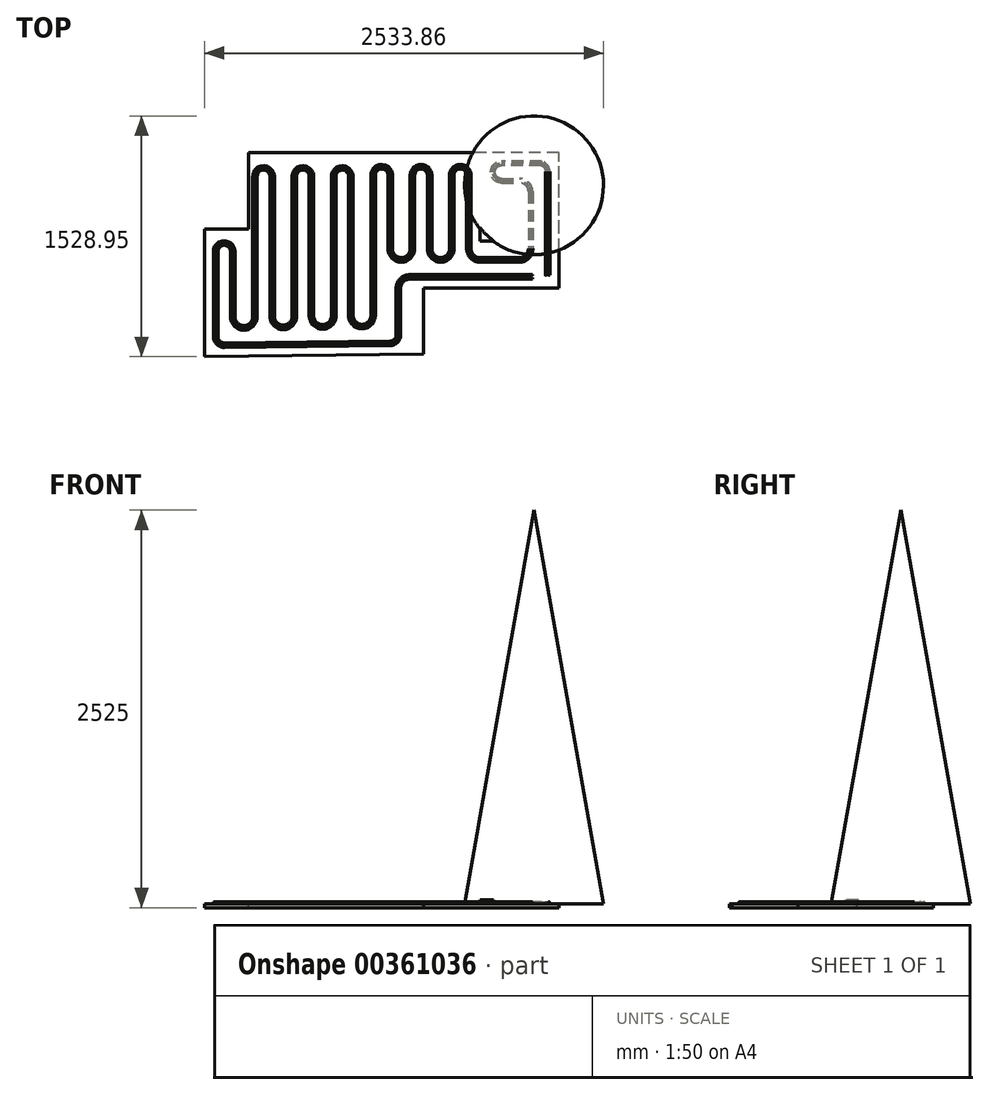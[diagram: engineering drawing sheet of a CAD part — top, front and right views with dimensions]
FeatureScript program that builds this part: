
annotation { "Feature Type Name" : "Feature", "Feature Type Description" : "" }
export const myFeature = defineFeature(function(context is Context, id is Id, definition is map)
    precondition{}
    {
        {
            var Q0;
            Q0=qCreatedBy(makeId("Top.planeOp"),FACE);
            var sketch = newSketch(context, id + "F0", { "sketchPlane" : qUnion([Q0])});
            skLineSegment(sketch, "E0", {"start": v(0, 0) * mm, "end": v(-1970, 0) * mm});
            skLineSegment(sketch, "E1", {"start": v(-1970, 0) * mm, "end": v(-1970, -485) * mm});
            skLineSegment(sketch, "E2", {"start": v(-1970, -485) * mm, "end": v(-2250, -485) * mm});
            skLineSegment(sketch, "E3", {"start": v(-2250, -485) * mm, "end": v(-2250, -1295) * mm});
            skLineSegment(sketch, "E4", {"start": v(-2250, -1295) * mm, "end": v(-860, -1280) * mm});
            skLineSegment(sketch, "E5", {"start": v(-860, -1280) * mm, "end": v(-860, -860) * mm});
            skLineSegment(sketch, "E6", {"start": v(-860, -860) * mm, "end": v(0, -860) * mm});
            skLineSegment(sketch, "E7", {"start": v(0, -860) * mm, "end": v(0, 0) * mm});
            skSolve(sketch);
        }
        {
            var Q0;
            Q0=makeQuery(id+"F0.imprint","IMPRINT",FACE,{"disambiguationData":[TD([[makeQuery(id+"F0.imprint","IMPRINT",EDGE,{"derivedFrom":sQuery(id+"F0.wireOp",EDGE,"E0")}),1.0]])]});
            extrude(context, id + "F1", {"entities" : qUnion([Q0]), "oppositeDirection" : true, "depth" : 25 * mm});
        }
        {
            var Q0;
            Q0=makeQuery(id+"F1.opExtrude","CAP_FACE",FACE,{"disambiguationData":[OSD([sQuery(id+"F0.wireOp",EDGE,"E0"),sQuery(id+"F0.wireOp",EDGE,"E1"),sQuery(id+"F0.wireOp",EDGE,"E2"),sQuery(id+"F0.wireOp",EDGE,"E3"),sQuery(id+"F0.wireOp",EDGE,"E4"),sQuery(id+"F0.wireOp",EDGE,"E5"),sQuery(id+"F0.wireOp",EDGE,"E6"),sQuery(id+"F0.wireOp",EDGE,"E7")])],"isStart":true});
            var sketch = newSketch(context, id + "F2", { "sketchPlane" : qUnion([Q0])});
            skLineSegment(sketch, "E8", {"start": v(-62.5, -1293.51) * mm, "end": v(-62.5, 0) * mm, "construction": true});
            skLineSegment(sketch, "E9.1.0.0", {"start": v(-187.5, -1293.51) * mm, "end": v(-187.5, 0) * mm, "construction": true});
            skLineSegment(sketch, "E9.2.0.0", {"start": v(-312.5, -1293.51) * mm, "end": v(-312.5, 0) * mm, "construction": true});
            skLineSegment(sketch, "E9.3.0.0", {"start": v(-437.5, -1293.51) * mm, "end": v(-437.5, 0) * mm, "construction": true});
            skLineSegment(sketch, "E9.4.0.0", {"start": v(-562.5, -1293.51) * mm, "end": v(-562.5, 0) * mm, "construction": true});
            skLineSegment(sketch, "E9.5.0.0", {"start": v(-687.5, -1293.51) * mm, "end": v(-687.5, 0) * mm, "construction": true});
            skLineSegment(sketch, "E9.6.0.0", {"start": v(-812.5, -1293.51) * mm, "end": v(-812.5, 0) * mm, "construction": true});
            skLineSegment(sketch, "E9.7.0.0", {"start": v(-937.5, -1293.51) * mm, "end": v(-937.5, 0) * mm, "construction": true});
            skLineSegment(sketch, "E9.8.0.0", {"start": v(-1062.5, -1293.51) * mm, "end": v(-1062.5, 0) * mm, "construction": true});
            skLineSegment(sketch, "E9.9.0.0", {"start": v(-1187.5, -1293.51) * mm, "end": v(-1187.5, 0) * mm, "construction": true});
            skLineSegment(sketch, "E9.10.0.0", {"start": v(-1312.5, -1293.51) * mm, "end": v(-1312.5, 0) * mm, "construction": true});
            skLineSegment(sketch, "E9.11.0.0", {"start": v(-1437.5, -1293.51) * mm, "end": v(-1437.5, 0) * mm, "construction": true});
            skLineSegment(sketch, "E9.12.0.0", {"start": v(-1562.5, -1293.51) * mm, "end": v(-1562.5, 0) * mm, "construction": true});
            skLineSegment(sketch, "E9.13.0.0", {"start": v(-1687.5, -1293.51) * mm, "end": v(-1687.5, 0) * mm, "construction": true});
            skLineSegment(sketch, "E9.14.0.0", {"start": v(-1812.5, -1293.51) * mm, "end": v(-1812.5, 0) * mm, "construction": true});
            skLineSegment(sketch, "E9.15.0.0", {"start": v(-1937.5, -1293.51) * mm, "end": v(-1937.5, 0) * mm, "construction": true});
            skLineSegment(sketch, "E9.16.0.0", {"start": v(-2062.5, -1293.51) * mm, "end": v(-2062.5, 0) * mm, "construction": true});
            skLineSegment(sketch, "E9.17.0.0", {"start": v(-2187.5, -1293.51) * mm, "end": v(-2187.5, 0) * mm, "construction": true});
            skLineSegment(sketch, "E9.18.0.0", {"start": v(-2312.5, -1293.51) * mm, "end": v(-2312.5, 0) * mm, "construction": true});
            skLineSegment(sketch, "E9.19.0.0", {"start": v(-2437.5, -1293.51) * mm, "end": v(-2437.5, 0) * mm, "construction": true});
            skLineSegment(sketch, "E9.direction1", {"start": v(-62.5, -1293.51) * mm, "end": v(-187.5, -1293.51) * mm, "construction": true});
            skLineSegment(sketch, "E10", {"start": v(0, -62.5) * mm, "end": v(-2437.5, -62.5) * mm, "construction": true});
            skLineSegment(sketch, "E11.0.1.0", {"start": v(0, -187.5) * mm, "end": v(-2437.5, -187.5) * mm, "construction": true});
            skLineSegment(sketch, "E11.0.2.0", {"start": v(0, -312.5) * mm, "end": v(-2437.5, -312.5) * mm, "construction": true});
            skLineSegment(sketch, "E11.0.3.0", {"start": v(0, -437.5) * mm, "end": v(-2437.5, -437.5) * mm, "construction": true});
            skLineSegment(sketch, "E11.0.4.0", {"start": v(0, -562.5) * mm, "end": v(-2437.5, -562.5) * mm, "construction": true});
            skLineSegment(sketch, "E11.0.5.0", {"start": v(0, -687.5) * mm, "end": v(-2437.5, -687.5) * mm, "construction": true});
            skLineSegment(sketch, "E11.0.6.0", {"start": v(0, -812.5) * mm, "end": v(-2437.5, -812.5) * mm, "construction": true});
            skLineSegment(sketch, "E11.0.7.0", {"start": v(0, -937.5) * mm, "end": v(-2437.5, -937.5) * mm, "construction": true});
            skLineSegment(sketch, "E11.0.8.0", {"start": v(0, -1062.5) * mm, "end": v(-2437.5, -1062.5) * mm, "construction": true});
            skLineSegment(sketch, "E11.0.9.0", {"start": v(0, -1187.5) * mm, "end": v(-2437.5, -1187.5) * mm, "construction": true});
            skLineSegment(sketch, "E11.direction1", {"start": v(-2437.5, -62.5) * mm, "end": v(-2410, -62.5) * mm, "construction": true});
            skLineSegment(sketch, "E11.direction2", {"start": v(-2437.5, -62.5) * mm, "end": v(-2437.5, -187.5) * mm, "construction": true});
            skLineSegment(sketch, "E12", {"start": v(-62.5, -937.5) * mm, "end": v(-62.5, -62.5) * mm});
            skLineSegment(sketch, "E13", {"start": v(-437.5, -672.5) * mm, "end": v(-562.5, -672.5) * mm});
            skLineSegment(sketch, "E14", {"start": v(-562.5, -672.5) * mm, "end": v(-562.5, -62.5) * mm});
            skLineSegment(sketch, "E15", {"start": v(-562.5, -62.5) * mm, "end": v(-687.5, -62.5) * mm});
            skLineSegment(sketch, "E16", {"start": v(-687.5, -62.5) * mm, "end": v(-687.5, -672.5) * mm});
            skLineSegment(sketch, "E17", {"start": v(-687.5, -672.5) * mm, "end": v(-812.5, -672.5) * mm});
            skLineSegment(sketch, "E18", {"start": v(-812.5, -672.5) * mm, "end": v(-812.5, -62.5) * mm});
            skLineSegment(sketch, "E19", {"start": v(-812.5, -62.5) * mm, "end": v(-937.5, -62.5) * mm});
            skLineSegment(sketch, "E20", {"start": v(-937.5, -62.5) * mm, "end": v(-937.5, -672.5) * mm});
            skLineSegment(sketch, "E21", {"start": v(-937.5, -672.5) * mm, "end": v(-1062.5, -672.5) * mm});
            skLineSegment(sketch, "E22", {"start": v(-1062.5, -672.5) * mm, "end": v(-1062.5, -62.5) * mm});
            skLineSegment(sketch, "E23", {"start": v(-1062.5, -62.5) * mm, "end": v(-1187.5, -62.5) * mm});
            skLineSegment(sketch, "E24", {"start": v(-1187.5, -62.5) * mm, "end": v(-1187.5, -1096.02) * mm});
            skLineSegment(sketch, "E25", {"start": v(-1187.5, -1096.02) * mm, "end": v(-1312.5, -1096.02) * mm});
            skLineSegment(sketch, "E26", {"start": v(-1312.5, -1096.02) * mm, "end": v(-1312.5, -62.5) * mm});
            skLineSegment(sketch, "E27", {"start": v(-1312.5, -62.5) * mm, "end": v(-1437.5, -62.5) * mm});
            skLineSegment(sketch, "E28", {"start": v(-1437.5, -62.5) * mm, "end": v(-1437.5, -1098.72) * mm});
            skLineSegment(sketch, "E29", {"start": v(-1437.5, -1098.72) * mm, "end": v(-1562.5, -1098.72) * mm});
            skLineSegment(sketch, "E30", {"start": v(-1562.5, -1098.72) * mm, "end": v(-1562.5, -62.5) * mm});
            skLineSegment(sketch, "E31", {"start": v(-1562.5, -62.5) * mm, "end": v(-1687.5, -62.5) * mm});
            skLineSegment(sketch, "E32", {"start": v(-1687.5, -62.5) * mm, "end": v(-1687.5, -1101.42) * mm});
            skLineSegment(sketch, "E33", {"start": v(-1687.5, -1101.42) * mm, "end": v(-1812.5, -1101.42) * mm});
            skLineSegment(sketch, "E34", {"start": v(-1812.5, -1101.42) * mm, "end": v(-1812.5, -62.5) * mm});
            skLineSegment(sketch, "E35", {"start": v(-1812.5, -62.5) * mm, "end": v(-1937.5, -62.5) * mm});
            skLineSegment(sketch, "E36", {"start": v(-1937.5, -62.5) * mm, "end": v(-1937.5, -1104.12) * mm});
            skLineSegment(sketch, "E37", {"start": v(-1937.5, -1104.12) * mm, "end": v(-2062.5, -1104.12) * mm});
            skLineSegment(sketch, "E38", {"start": v(-2062.5, -547.5) * mm, "end": v(-2187.5, -547.5) * mm});
            skLineSegment(sketch, "E39", {"start": v(-2187.5, -547.5) * mm, "end": v(-2187.5, -1231.82) * mm});
            skLineSegment(sketch, "E40", {"start": v(-2187.5, -1231.82) * mm, "end": v(-1010, -1219.12) * mm});
            skLineSegment(sketch, "E41", {"start": v(-1010, -1219.12) * mm, "end": v(-1010, -797.5) * mm});
            skLineSegment(sketch, "E42", {"start": v(-1010, -797.5) * mm, "end": v(-187.5, -797.5) * mm});
            skLineSegment(sketch, "E43", {"start": v(-187.5, -797.5) * mm, "end": v(-187.5, -937.5) * mm});
            skLineSegment(sketch, "E44", {"start": v(-2062.5, -547.5) * mm, "end": v(-2062.5, -1104.12) * mm});
            skLineSegment(sketch, "E45", {"start": v(-62.5, -62.5) * mm, "end": v(-437.5, -62.5) * mm});
            skLineSegment(sketch, "E46", {"start": v(-437.5, -62.5) * mm, "end": v(-437.5, -187.5) * mm});
            skLineSegment(sketch, "E47", {"start": v(-437.5, -187.5) * mm, "end": v(-187.5, -187.5) * mm});
            skLineSegment(sketch, "E48", {"start": v(-187.5, -187.5) * mm, "end": v(-187.5, -672.5) * mm});
            skLineSegment(sketch, "E49", {"start": v(-187.5, -672.5) * mm, "end": v(-437.5, -672.5) * mm});
            skSolve(sketch);
        }
        {
            var Q0;
            {var subQ0=sQuery(id+"F2.wireOp",EDGE,"o94TWT2M-31Vf-qluU-QspM-yvdoEJApc5KK");Q0=makeQuery(id+"F2.imprint","IMPRINT",FACE,{"disambiguationData":[TD([[makeQuery(id+"F2.imprint","IMPRINT",EDGE,{"derivedFrom":subQ0}),1.0]])]});}
            var Q1;
            Q1 = qConstructionFilter(qBodyType(qCreatedBy(id + "F2" ,EDGE), BodyType.WIRE), ConstructionObject.NO);
            extrude(context, id + "F3", {"entities" : qUnion([Q0]), "bodyType" : ExtendedToolBodyType.SURFACE, "surfaceEntities" : qUnion([Q1]), "depth" : 12 * mm});
        }
        {
            var Q0;
            Q0=makeQuery(id+"F3.opExtrude","SWEPT_EDGE",EDGE,{"disambiguationData":[OSD([sQuery(id+"F2.wireOp",VERTEX,"o94TWT2M-31Vf-qluU-QspM-yvdoEJApc5KK.start")])]});
            var Q1;
            Q1=makeQuery(id+"F3.opExtrude","SWEPT_EDGE",EDGE,{"disambiguationData":[OSD([sQuery(id+"F2.wireOp",VERTEX,"3uiTuNdA-6T9n-bDHV-g5J5-OovVtDSzKxf0.start")])]});
            var Q2;
            Q2=makeQuery(id+"F3.opExtrude","SWEPT_EDGE",EDGE,{"disambiguationData":[OSD([sQuery(id+"F2.wireOp",VERTEX,"RiOLPlBG-YKD5-Dv3i-Ig6h-eSt2upFAfSOZ.start")])]});
            var Q3;
            Q3=makeQuery(id+"F3.opExtrude","SWEPT_EDGE",EDGE,{"disambiguationData":[OSD([sQuery(id+"F2.wireOp",VERTEX,"fgvgJ5WA-tqRb-h4RY-nfcN-i2yzFQp1ZdVO.start")])]});
            var Q4;
            Q4=makeQuery(id+"F3.opExtrude","SWEPT_EDGE",EDGE,{"disambiguationData":[OSD([sQuery(id+"F2.wireOp",VERTEX,"E15.start")])]});
            var Q5;
            Q5=makeQuery(id+"F3.opExtrude","SWEPT_EDGE",EDGE,{"disambiguationData":[OSD([sQuery(id+"F2.wireOp",VERTEX,"E16.start")])]});
            var Q6;
            Q6=makeQuery(id+"F3.opExtrude","SWEPT_EDGE",EDGE,{"disambiguationData":[OSD([sQuery(id+"F2.wireOp",VERTEX,"E19.start")])]});
            var Q7;
            Q7=makeQuery(id+"F3.opExtrude","SWEPT_EDGE",EDGE,{"disambiguationData":[OSD([sQuery(id+"F2.wireOp",VERTEX,"E20.start")])]});
            var Q8;
            Q8=makeQuery(id+"F3.opExtrude","SWEPT_EDGE",EDGE,{"disambiguationData":[OSD([sQuery(id+"F2.wireOp",VERTEX,"E23.start")])]});
            var Q9;
            Q9=makeQuery(id+"F3.opExtrude","SWEPT_EDGE",EDGE,{"disambiguationData":[OSD([sQuery(id+"F2.wireOp",VERTEX,"E24.start")])]});
            var Q10;
            Q10=makeQuery(id+"F3.opExtrude","SWEPT_EDGE",EDGE,{"disambiguationData":[OSD([sQuery(id+"F2.wireOp",VERTEX,"E27.start")])]});
            var Q11;
            Q11=makeQuery(id+"F3.opExtrude","SWEPT_EDGE",EDGE,{"disambiguationData":[OSD([sQuery(id+"F2.wireOp",VERTEX,"E28.start")])]});
            var Q12;
            Q12=makeQuery(id+"F3.opExtrude","SWEPT_EDGE",EDGE,{"disambiguationData":[OSD([sQuery(id+"F2.wireOp",VERTEX,"E31.start")])]});
            var Q13;
            Q13=makeQuery(id+"F3.opExtrude","SWEPT_EDGE",EDGE,{"disambiguationData":[OSD([sQuery(id+"F2.wireOp",VERTEX,"E32.start")])]});
            var Q14;
            Q14=makeQuery(id+"F3.opExtrude","SWEPT_EDGE",EDGE,{"disambiguationData":[OSD([sQuery(id+"F2.wireOp",VERTEX,"E35.start")])]});
            var Q15;
            Q15=makeQuery(id+"F3.opExtrude","SWEPT_EDGE",EDGE,{"disambiguationData":[OSD([sQuery(id+"F2.wireOp",VERTEX,"E36.start")])]});
            var Q16;
            Q16=makeQuery(id+"F3.opExtrude","SWEPT_EDGE",EDGE,{"disambiguationData":[OSD([sQuery(id+"F2.wireOp",VERTEX,"E44.start")])]});
            var Q17;
            Q17=makeQuery(id+"F3.opExtrude","SWEPT_EDGE",EDGE,{"disambiguationData":[OSD([sQuery(id+"F2.wireOp",VERTEX,"E39.start")])]});
            var Q18;
            Q18=makeQuery(id+"F3.opExtrude","SWEPT_EDGE",EDGE,{"disambiguationData":[OSD([sQuery(id+"F2.wireOp",VERTEX,"qBJzUNNh-qAKs-Ri77-QN58-BEaqMge8Y34i.start")])]});
            var Q19;
            Q19=makeQuery(id+"F3.opExtrude","SWEPT_EDGE",EDGE,{"disambiguationData":[OSD([sQuery(id+"F2.wireOp",VERTEX,"nYMLm4uN-mVzM-m0Mm-nZ4a-ShaaZ95DERLO.start")])]});
            var Q20;
            Q20=makeQuery(id+"F3.opExtrude","SWEPT_EDGE",EDGE,{"disambiguationData":[OSD([sQuery(id+"F2.wireOp",VERTEX,"E13.start")])]});
            var Q21;
            Q21=makeQuery(id+"F3.opExtrude","SWEPT_EDGE",EDGE,{"disambiguationData":[OSD([sQuery(id+"F2.wireOp",VERTEX,"E14.start")])]});
            var Q22;
            Q22=makeQuery(id+"F3.opExtrude","SWEPT_EDGE",EDGE,{"disambiguationData":[OSD([sQuery(id+"F2.wireOp",VERTEX,"E17.start")])]});
            var Q23;
            Q23=makeQuery(id+"F3.opExtrude","SWEPT_EDGE",EDGE,{"disambiguationData":[OSD([sQuery(id+"F2.wireOp",VERTEX,"E18.start")])]});
            var Q24;
            Q24=makeQuery(id+"F3.opExtrude","SWEPT_EDGE",EDGE,{"disambiguationData":[OSD([sQuery(id+"F2.wireOp",VERTEX,"E21.start")])]});
            var Q25;
            Q25=makeQuery(id+"F3.opExtrude","SWEPT_EDGE",EDGE,{"disambiguationData":[OSD([sQuery(id+"F2.wireOp",VERTEX,"E22.start")])]});
            var Q26;
            Q26=makeQuery(id+"F3.opExtrude","SWEPT_EDGE",EDGE,{"disambiguationData":[OSD([sQuery(id+"F2.wireOp",VERTEX,"E25.start")])]});
            var Q27;
            Q27=makeQuery(id+"F3.opExtrude","SWEPT_EDGE",EDGE,{"disambiguationData":[OSD([sQuery(id+"F2.wireOp",VERTEX,"E41.start")])]});
            var Q28;
            Q28=makeQuery(id+"F3.opExtrude","SWEPT_EDGE",EDGE,{"disambiguationData":[OSD([sQuery(id+"F2.wireOp",VERTEX,"E42.start")])]});
            var Q29;
            Q29=makeQuery(id+"F3.opExtrude","SWEPT_EDGE",EDGE,{"disambiguationData":[OSD([sQuery(id+"F2.wireOp",VERTEX,"E43.start")])]});
            var Q30;
            Q30=makeQuery(id+"F3.opExtrude","SWEPT_EDGE",EDGE,{"disambiguationData":[OSD([sQuery(id+"F2.wireOp",VERTEX,"E26.start")])]});
            var Q31;
            Q31=makeQuery(id+"F3.opExtrude","SWEPT_EDGE",EDGE,{"disambiguationData":[OSD([sQuery(id+"F2.wireOp",VERTEX,"E29.start")])]});
            var Q32;
            Q32=makeQuery(id+"F3.opExtrude","SWEPT_EDGE",EDGE,{"disambiguationData":[OSD([sQuery(id+"F2.wireOp",VERTEX,"E30.start")])]});
            var Q33;
            Q33=makeQuery(id+"F3.opExtrude","SWEPT_EDGE",EDGE,{"disambiguationData":[OSD([sQuery(id+"F2.wireOp",VERTEX,"E33.start")])]});
            var Q34;
            Q34=makeQuery(id+"F3.opExtrude","SWEPT_EDGE",EDGE,{"disambiguationData":[OSD([sQuery(id+"F2.wireOp",VERTEX,"E34.start")])]});
            var Q35;
            Q35=makeQuery(id+"F3.opExtrude","SWEPT_EDGE",EDGE,{"disambiguationData":[OSD([sQuery(id+"F2.wireOp",VERTEX,"E37.start")])]});
            var Q36;
            Q36=makeQuery(id+"F3.opExtrude","SWEPT_EDGE",EDGE,{"disambiguationData":[OSD([sQuery(id+"F2.wireOp",VERTEX,"E44.end")])]});
            var Q37;
            Q37=makeQuery(id+"F3.opExtrude","SWEPT_EDGE",EDGE,{"disambiguationData":[OSD([sQuery(id+"F2.wireOp",VERTEX,"E40.start")])]});
            var Q38;
            Q38=makeQuery(id+"F3.opExtrude","SWEPT_EDGE",EDGE,{"disambiguationData":[OSD([sQuery(id+"F2.wireOp",VERTEX,"E49.start")])]});
            var Q39;
            Q39=makeQuery(id+"F3.opExtrude","SWEPT_EDGE",EDGE,{"disambiguationData":[OSD([sQuery(id+"F2.wireOp",VERTEX,"E48.start")])]});
            var Q40;
            Q40=makeQuery(id+"F3.opExtrude","SWEPT_EDGE",EDGE,{"disambiguationData":[OSD([sQuery(id+"F2.wireOp",VERTEX,"E47.start")])]});
            var Q41;
            Q41=makeQuery(id+"F3.opExtrude","SWEPT_EDGE",EDGE,{"disambiguationData":[OSD([sQuery(id+"F2.wireOp",VERTEX,"E46.start")])]});
            var Q42;
            Q42=makeQuery(id+"F3.opExtrude","SWEPT_EDGE",EDGE,{"disambiguationData":[OSD([sQuery(id+"F2.wireOp",VERTEX,"E45.start")])]});
            fillet(context, id + "F4", {"entities" : qUnion([Q0, Q1, Q2, Q3, Q4, Q5, Q6, Q7, Q8, Q9, Q10, Q11, Q12, Q13, Q14, Q15, Q16, Q17, Q18, Q19, Q20, Q21, Q22, Q23, Q24, Q25, Q26, Q27, Q28, Q29, Q30, Q31, Q32, Q33, Q34, Q35, Q36, Q37, Q38, Q39, Q40, Q41, Q42]), "radius" : (125 / 2) * mm, "tangentPropagation" : true, "allowEdgeOverflow" : false});
        }
        {
            var Q0;
            Q0=makeQuery(id+"F1.opExtrude","CAP_FACE",FACE,{"disambiguationData":[OSD([sQuery(id+"F0.wireOp",EDGE,"E0"),sQuery(id+"F0.wireOp",EDGE,"E1"),sQuery(id+"F0.wireOp",EDGE,"E2"),sQuery(id+"F0.wireOp",EDGE,"E3"),sQuery(id+"F0.wireOp",EDGE,"E4"),sQuery(id+"F0.wireOp",EDGE,"E5"),sQuery(id+"F0.wireOp",EDGE,"E6"),sQuery(id+"F0.wireOp",EDGE,"E7")])],"isStart":true});
            cPlane(context, id + "F5", {"entities" : qUnion([Q0]), "cplaneType" : CPlaneType.OFFSET, "offset" : 2.5 * mm, "width" : 150 * mm, "height" : 150 * mm});
        }
        {
            var Q0;
            Q0=qCreatedBy(id+"F5.planeOp",FACE);
            var sketch = newSketch(context, id + "F6", { "sketchPlane" : qUnion([Q0])});
            skLineSegment(sketch, "E50.0", {"start": v(-82.5, -119.72) * mm, "end": v(-82.5, -777.5) * mm});
            skArc(sketch, "E50.1", {"start": v(-112.72, -79.03) * mm, "mid": v(-90.88, -94.38) * mm, "end": v(-82.5, -119.72) * mm});
            skLineSegment(sketch, "E50.2", {"start": v(-167.5, -610) * mm, "end": v(-167.5, -248.35) * mm});
            skLineSegment(sketch, "E50.8", {"start": v(-582.5, -142.5) * mm, "end": v(-582.5, -610) * mm});
            skArc(sketch, "E50.9", {"start": v(-667.5, -142.5) * mm, "mid": v(-625, -100) * mm, "end": v(-582.5, -142.5) * mm});
            skLineSegment(sketch, "E50.10", {"start": v(-667.5, -610) * mm, "end": v(-667.5, -142.5) * mm});
            skArc(sketch, "E50.11", {"start": v(-832.5, -610) * mm, "mid": v(-750, -692.5) * mm, "end": v(-667.5, -610) * mm});
            skLineSegment(sketch, "E50.12", {"start": v(-832.5, -142.5) * mm, "end": v(-832.5, -610) * mm});
            skArc(sketch, "E50.13", {"start": v(-917.5, -142.5) * mm, "mid": v(-875, -100) * mm, "end": v(-832.5, -142.5) * mm});
            skLineSegment(sketch, "E50.14", {"start": v(-917.5, -610) * mm, "end": v(-917.5, -142.5) * mm});
            skArc(sketch, "E50.15", {"start": v(-1082.5, -610) * mm, "mid": v(-1000, -692.5) * mm, "end": v(-917.5, -610) * mm});
            skLineSegment(sketch, "E50.16", {"start": v(-1082.5, -142.5) * mm, "end": v(-1082.5, -610) * mm});
            skArc(sketch, "E50.17", {"start": v(-1167.5, -142.5) * mm, "mid": v(-1125, -100) * mm, "end": v(-1082.5, -142.5) * mm});
            skLineSegment(sketch, "E50.18", {"start": v(-1167.5, -1033.52) * mm, "end": v(-1167.5, -142.5) * mm});
            skArc(sketch, "E50.19", {"start": v(-1332.5, -1033.52) * mm, "mid": v(-1250, -1116.02) * mm, "end": v(-1167.5, -1033.52) * mm});
            skLineSegment(sketch, "E50.20", {"start": v(-1332.5, -150) * mm, "end": v(-1332.5, -1033.52) * mm});
            skArc(sketch, "E50.21", {"start": v(-2167.5, -627.5) * mm, "mid": v(-2125, -585) * mm, "end": v(-2082.5, -627.5) * mm});
            skLineSegment(sketch, "E50.22", {"start": v(-2167.5, -1167.97) * mm, "end": v(-2167.5, -627.5) * mm});
            skArc(sketch, "E50.23", {"start": v(-2124.54, -1210.47) * mm, "mid": v(-2154.89, -1198.19) * mm, "end": v(-2167.5, -1167.97) * mm});
            skLineSegment(sketch, "E50.24", {"start": v(-1072.04, -1199.11) * mm, "end": v(-2124.54, -1210.47) * mm});
            skArc(sketch, "E50.25", {"start": v(-1030, -1156.62) * mm, "mid": v(-1042.29, -1186.5) * mm, "end": v(-1072.04, -1199.11) * mm});
            skLineSegment(sketch, "E50.26", {"start": v(-1030, -860) * mm, "end": v(-1030, -1156.62) * mm});
            skLineSegment(sketch, "E50.29", {"start": v(-167.5, -777.5) * mm, "end": v(-947.5, -777.5) * mm});
            skArc(sketch, "E50.30", {"start": v(-947.5, -777.5) * mm, "mid": v(-1005.84, -801.66) * mm, "end": v(-1030, -860) * mm});
            skLineSegment(sketch, "E50.31", {"start": v(-2082.5, -1041.62) * mm, "end": v(-2082.5, -627.5) * mm});
            skArc(sketch, "E50.32", {"start": v(-2082.5, -1041.62) * mm, "mid": v(-2000, -1124.12) * mm, "end": v(-1917.5, -1041.62) * mm});
            skLineSegment(sketch, "E50.33", {"start": v(-1917.5, -1041.62) * mm, "end": v(-1917.5, -150) * mm});
            skArc(sketch, "E50.34", {"start": v(-1917.5, -150) * mm, "mid": v(-1875, -107.5) * mm, "end": v(-1832.5, -150) * mm});
            skLineSegment(sketch, "E50.35", {"start": v(-1832.5, -150) * mm, "end": v(-1832.5, -1038.92) * mm});
            skArc(sketch, "E50.36", {"start": v(-1832.5, -1038.92) * mm, "mid": v(-1750, -1121.42) * mm, "end": v(-1667.5, -1038.92) * mm});
            skLineSegment(sketch, "E50.37", {"start": v(-1667.5, -1038.92) * mm, "end": v(-1667.5, -150) * mm});
            skArc(sketch, "E50.38", {"start": v(-1667.5, -150) * mm, "mid": v(-1625, -107.5) * mm, "end": v(-1582.5, -150) * mm});
            skLineSegment(sketch, "E50.39", {"start": v(-1582.5, -150) * mm, "end": v(-1582.5, -1036.22) * mm});
            skArc(sketch, "E50.40", {"start": v(-1582.5, -1036.22) * mm, "mid": v(-1500, -1118.72) * mm, "end": v(-1417.5, -1036.22) * mm});
            skLineSegment(sketch, "E50.41", {"start": v(-1417.5, -1036.22) * mm, "end": v(-1417.5, -150) * mm});
            skArc(sketch, "E50.42", {"start": v(-1417.5, -150) * mm, "mid": v(-1375, -107.5) * mm, "end": v(-1332.5, -150) * mm});
            skLineSegment(sketch, "E51", {"start": v(-82.5, -777.5) * mm, "end": v(-82.5, -1008.77) * mm, "construction": true});
            skLineSegment(sketch, "E52", {"start": v(-500, -692.5) * mm, "end": v(-250, -692.5) * mm});
            skPoint(sketch, "E52.startSnap0", {"position": v(-750, -692.5) * mm});
            skLineSegment(sketch, "E53", {"start": v(-112.72, -79.03) * mm, "end": v(-363.95, -79.03) * mm});
            skLineSegment(sketch, "E54", {"start": v(-406.45, -121.53) * mm, "end": v(-406.45, -123.35) * mm});
            skLineSegment(sketch, "E55", {"start": v(-363.95, -165.85) * mm, "end": v(-250, -165.85) * mm});
            skPoint(sketch, "E56.visualSharp", {"position": v(-582.5, -692.5) * mm});
            skArc(sketch, "E56.filletArc", {"start": v(-582.5, -610) * mm, "mid": v(-558.34, -668.34) * mm, "end": v(-500, -692.5) * mm});
            skPoint(sketch, "E57.visualSharp", {"position": v(-167.5, -692.5) * mm});
            skArc(sketch, "E57.filletArc", {"start": v(-250, -692.5) * mm, "mid": v(-191.66, -668.34) * mm, "end": v(-167.5, -610) * mm});
            skPoint(sketch, "E58.visualSharp", {"position": v(-167.5, -165.85) * mm});
            skArc(sketch, "E58.filletArc", {"start": v(-167.5, -248.35) * mm, "mid": v(-191.66, -190) * mm, "end": v(-250, -165.85) * mm});
            skPoint(sketch, "E59.visualSharp", {"position": v(-406.45, -165.85) * mm});
            skArc(sketch, "E59.filletArc", {"start": v(-406.45, -123.35) * mm, "mid": v(-394, -153.4) * mm, "end": v(-363.95, -165.85) * mm});
            skPoint(sketch, "E60.visualSharp", {"position": v(-406.45, -79.03) * mm});
            skArc(sketch, "E60.filletArc", {"start": v(-363.95, -79.03) * mm, "mid": v(-394, -91.48) * mm, "end": v(-406.45, -121.53) * mm});
            skSolve(sketch);
        }
        {
            var Q0;
            Q0=makeQuery(id+"F1.opExtrude","CAP_FACE",FACE,{"disambiguationData":[OSD([sQuery(id+"F0.wireOp",EDGE,"E0"),sQuery(id+"F0.wireOp",EDGE,"E1"),sQuery(id+"F0.wireOp",EDGE,"E2"),sQuery(id+"F0.wireOp",EDGE,"E3"),sQuery(id+"F0.wireOp",EDGE,"E4"),sQuery(id+"F0.wireOp",EDGE,"E5"),sQuery(id+"F0.wireOp",EDGE,"E6"),sQuery(id+"F0.wireOp",EDGE,"E7")])],"isStart":true});
            cPlane(context, id + "F7", {"entities" : qUnion([Q0]), "cplaneType" : CPlaneType.OFFSET, "offset" : 6 * mm, "width" : 150 * mm, "height" : 150 * mm});
        }
        {
            var Q0;
            Q0=qCreatedBy(id+"F7.planeOp",FACE);
            var sketch = newSketch(context, id + "F8", { "sketchPlane" : qUnion([Q0])});
            skArc(sketch, "E61.0.1", {"start": v(-62.5, -125) * mm, "mid": v(-125, -62.5) * mm, "end": v(-187.5, -125) * mm});
            skArc(sketch, "E61.0.3", {"start": v(-187.5, -125) * mm, "mid": v(-125, -62.5) * mm, "end": v(-62.5, -125) * mm});
            skArc(sketch, "E61.1.1", {"start": v(-187.5, -550) * mm, "mid": v(-250, -612.5) * mm, "end": v(-312.5, -550) * mm});
            skArc(sketch, "E61.1.3", {"start": v(-312.5, -550) * mm, "mid": v(-250, -612.5) * mm, "end": v(-187.5, -550) * mm});
            skArc(sketch, "E61.2.1", {"start": v(-312.5, -125) * mm, "mid": v(-375, -62.5) * mm, "end": v(-437.5, -125) * mm});
            skArc(sketch, "E61.2.3", {"start": v(-437.5, -125) * mm, "mid": v(-375, -62.5) * mm, "end": v(-312.5, -125) * mm});
            skArc(sketch, "E61.3.1", {"start": v(-437.5, -550) * mm, "mid": v(-500, -612.5) * mm, "end": v(-562.5, -550) * mm});
            skArc(sketch, "E61.3.3", {"start": v(-562.5, -550) * mm, "mid": v(-500, -612.5) * mm, "end": v(-437.5, -550) * mm});
            skArc(sketch, "E61.4.1", {"start": v(-562.5, -125) * mm, "mid": v(-625, -62.5) * mm, "end": v(-687.5, -125) * mm});
            skArc(sketch, "E61.4.3", {"start": v(-687.5, -125) * mm, "mid": v(-625, -62.5) * mm, "end": v(-562.5, -125) * mm});
            skArc(sketch, "E61.5.1", {"start": v(-687.5, -550) * mm, "mid": v(-750, -612.5) * mm, "end": v(-812.5, -550) * mm});
            skArc(sketch, "E61.5.3", {"start": v(-812.5, -550) * mm, "mid": v(-750, -612.5) * mm, "end": v(-687.5, -550) * mm});
            skArc(sketch, "E61.6.1", {"start": v(-812.5, -125) * mm, "mid": v(-875, -62.5) * mm, "end": v(-937.5, -125) * mm});
            skArc(sketch, "E61.6.3", {"start": v(-937.5, -125) * mm, "mid": v(-875, -62.5) * mm, "end": v(-812.5, -125) * mm});
            skArc(sketch, "E61.7.1", {"start": v(-937.5, -954.48) * mm, "mid": v(-1000, -1016.98) * mm, "end": v(-1062.5, -954.48) * mm});
            skArc(sketch, "E61.7.3", {"start": v(-1062.5, -954.48) * mm, "mid": v(-1000, -1016.98) * mm, "end": v(-937.5, -954.48) * mm});
            skArc(sketch, "E61.8.1", {"start": v(-1062.5, -125) * mm, "mid": v(-1125, -62.5) * mm, "end": v(-1187.5, -125) * mm});
            skArc(sketch, "E61.8.3", {"start": v(-1187.5, -125) * mm, "mid": v(-1125, -62.5) * mm, "end": v(-1062.5, -125) * mm});
            skArc(sketch, "E61.9.1", {"start": v(-1187.5, -962.81) * mm, "mid": v(-1250, -1025.31) * mm, "end": v(-1312.5, -962.81) * mm});
            skArc(sketch, "E61.9.3", {"start": v(-1312.5, -962.81) * mm, "mid": v(-1250, -1025.31) * mm, "end": v(-1187.5, -962.81) * mm});
            skArc(sketch, "E61.10.1", {"start": v(-1312.5, -125) * mm, "mid": v(-1375, -62.5) * mm, "end": v(-1437.5, -125) * mm});
            skArc(sketch, "E61.10.3", {"start": v(-1437.5, -125) * mm, "mid": v(-1375, -62.5) * mm, "end": v(-1312.5, -125) * mm});
            skArc(sketch, "E61.11.1", {"start": v(-1437.5, -971.15) * mm, "mid": v(-1500, -1033.65) * mm, "end": v(-1562.5, -971.15) * mm});
            skArc(sketch, "E61.11.3", {"start": v(-1562.5, -971.15) * mm, "mid": v(-1500, -1033.65) * mm, "end": v(-1437.5, -971.15) * mm});
            skArc(sketch, "E61.12.1", {"start": v(-1562.5, -125) * mm, "mid": v(-1625, -62.5) * mm, "end": v(-1687.5, -125) * mm});
            skArc(sketch, "E61.12.3", {"start": v(-1687.5, -125) * mm, "mid": v(-1625, -62.5) * mm, "end": v(-1562.5, -125) * mm});
            skArc(sketch, "E61.13.1", {"start": v(-1687.5, -979.48) * mm, "mid": v(-1750, -1041.98) * mm, "end": v(-1812.5, -979.48) * mm});
            skArc(sketch, "E61.13.3", {"start": v(-1812.5, -979.48) * mm, "mid": v(-1750, -1041.98) * mm, "end": v(-1687.5, -979.48) * mm});
            skArc(sketch, "E61.14.1", {"start": v(-1812.5, -125) * mm, "mid": v(-1875, -62.5) * mm, "end": v(-1937.5, -125) * mm});
            skArc(sketch, "E61.14.3", {"start": v(-1937.5, -125) * mm, "mid": v(-1875, -62.5) * mm, "end": v(-1812.5, -125) * mm});
            skArc(sketch, "E61.15.1", {"start": v(-1937.5, -987.81) * mm, "mid": v(-2000, -1050.31) * mm, "end": v(-2062.5, -987.81) * mm});
            skArc(sketch, "E61.15.3", {"start": v(-2062.5, -987.81) * mm, "mid": v(-2000, -1050.31) * mm, "end": v(-1937.5, -987.81) * mm});
            skArc(sketch, "E61.16.0", {"start": v(-2187.5, -610) * mm, "mid": v(-2125, -547.5) * mm, "end": v(-2062.5, -610) * mm});
            skArc(sketch, "E61.16.2", {"start": v(-2062.5, -610) * mm, "mid": v(-2125, -547.5) * mm, "end": v(-2187.5, -610) * mm});
            skArc(sketch, "E61.17.0", {"start": v(-2187.5, -1168.64) * mm, "mid": v(-2168.96, -1213.08) * mm, "end": v(-2124.33, -1231.14) * mm});
            skArc(sketch, "E61.17.2", {"start": v(-2124.33, -1231.14) * mm, "mid": v(-2168.96, -1213.08) * mm, "end": v(-2187.5, -1168.64) * mm});
            skArc(sketch, "E61.18.0", {"start": v(-1071.83, -1219.78) * mm, "mid": v(-1028.07, -1201.24) * mm, "end": v(-1010, -1157.29) * mm});
            skArc(sketch, "E61.18.2", {"start": v(-1010, -1157.29) * mm, "mid": v(-1028.07, -1201.24) * mm, "end": v(-1071.83, -1219.78) * mm});
            skArc(sketch, "E61.19.0", {"start": v(-1010, -860) * mm, "mid": v(-991.7, -815.8) * mm, "end": v(-947.5, -797.5) * mm});
            skArc(sketch, "E61.19.2", {"start": v(-947.5, -797.5) * mm, "mid": v(-991.7, -815.8) * mm, "end": v(-1010, -860) * mm});
            skArc(sketch, "E61.20.0", {"start": v(-250, -797.5) * mm, "mid": v(-205.8, -815.8) * mm, "end": v(-187.5, -860) * mm});
            skArc(sketch, "E61.20.2", {"start": v(-187.5, -860) * mm, "mid": v(-205.8, -815.8) * mm, "end": v(-250, -797.5) * mm});
            skLineSegment(sketch, "E61.21.0", {"start": v(-62.5, -937.5) * mm, "end": v(-62.5, -125) * mm});
            skLineSegment(sketch, "E61.21.2", {"start": v(-62.5, -125) * mm, "end": v(-62.5, -937.5) * mm});
            skLineSegment(sketch, "E61.22.0", {"start": v(-187.5, -125) * mm, "end": v(-187.5, -550) * mm});
            skLineSegment(sketch, "E61.22.2", {"start": v(-187.5, -550) * mm, "end": v(-187.5, -125) * mm});
            skLineSegment(sketch, "E61.23.0", {"start": v(-312.5, -550) * mm, "end": v(-312.5, -125) * mm});
            skLineSegment(sketch, "E61.23.2", {"start": v(-312.5, -125) * mm, "end": v(-312.5, -550) * mm});
            skLineSegment(sketch, "E61.24.0", {"start": v(-437.5, -125) * mm, "end": v(-437.5, -550) * mm});
            skLineSegment(sketch, "E61.24.2", {"start": v(-437.5, -550) * mm, "end": v(-437.5, -125) * mm});
            skLineSegment(sketch, "E61.25.0", {"start": v(-562.5, -550) * mm, "end": v(-562.5, -125) * mm});
            skLineSegment(sketch, "E61.25.2", {"start": v(-562.5, -125) * mm, "end": v(-562.5, -550) * mm});
            skLineSegment(sketch, "E61.26.0", {"start": v(-687.5, -125) * mm, "end": v(-687.5, -550) * mm});
            skLineSegment(sketch, "E61.26.2", {"start": v(-687.5, -550) * mm, "end": v(-687.5, -125) * mm});
            skLineSegment(sketch, "E61.27.0", {"start": v(-812.5, -550) * mm, "end": v(-812.5, -125) * mm});
            skLineSegment(sketch, "E61.27.2", {"start": v(-812.5, -125) * mm, "end": v(-812.5, -550) * mm});
            skLineSegment(sketch, "E61.28.0", {"start": v(-937.5, -125) * mm, "end": v(-937.5, -954.48) * mm});
            skLineSegment(sketch, "E61.28.2", {"start": v(-937.5, -954.48) * mm, "end": v(-937.5, -125) * mm});
            skLineSegment(sketch, "E61.29.0", {"start": v(-1062.5, -954.48) * mm, "end": v(-1062.5, -125) * mm});
            skLineSegment(sketch, "E61.29.2", {"start": v(-1062.5, -125) * mm, "end": v(-1062.5, -954.48) * mm});
            skLineSegment(sketch, "E61.30.0", {"start": v(-1187.5, -125) * mm, "end": v(-1187.5, -962.81) * mm});
            skLineSegment(sketch, "E61.30.2", {"start": v(-1187.5, -962.81) * mm, "end": v(-1187.5, -125) * mm});
            skLineSegment(sketch, "E61.31.0", {"start": v(-1312.5, -962.81) * mm, "end": v(-1312.5, -125) * mm});
            skLineSegment(sketch, "E61.31.2", {"start": v(-1312.5, -125) * mm, "end": v(-1312.5, -962.81) * mm});
            skLineSegment(sketch, "E61.32.0", {"start": v(-1437.5, -125) * mm, "end": v(-1437.5, -971.15) * mm});
            skLineSegment(sketch, "E61.32.2", {"start": v(-1437.5, -971.15) * mm, "end": v(-1437.5, -125) * mm});
            skLineSegment(sketch, "E61.33.0", {"start": v(-1562.5, -971.15) * mm, "end": v(-1562.5, -125) * mm});
            skLineSegment(sketch, "E61.33.2", {"start": v(-1562.5, -125) * mm, "end": v(-1562.5, -971.15) * mm});
            skLineSegment(sketch, "E61.34.0", {"start": v(-1687.5, -125) * mm, "end": v(-1687.5, -979.48) * mm});
            skLineSegment(sketch, "E61.34.2", {"start": v(-1687.5, -979.48) * mm, "end": v(-1687.5, -125) * mm});
            skLineSegment(sketch, "E61.35.0", {"start": v(-1812.5, -979.48) * mm, "end": v(-1812.5, -125) * mm});
            skLineSegment(sketch, "E61.35.2", {"start": v(-1812.5, -125) * mm, "end": v(-1812.5, -979.48) * mm});
            skLineSegment(sketch, "E61.36.0", {"start": v(-1937.5, -125) * mm, "end": v(-1937.5, -987.81) * mm});
            skLineSegment(sketch, "E61.36.2", {"start": v(-1937.5, -987.81) * mm, "end": v(-1937.5, -125) * mm});
            skLineSegment(sketch, "E61.37.0", {"start": v(-2187.5, -1168.64) * mm, "end": v(-2187.5, -610) * mm});
            skLineSegment(sketch, "E61.37.2", {"start": v(-2187.5, -610) * mm, "end": v(-2187.5, -1168.64) * mm});
            skLineSegment(sketch, "E61.38.0", {"start": v(-1071.83, -1219.78) * mm, "end": v(-2124.33, -1231.14) * mm});
            skLineSegment(sketch, "E61.38.2", {"start": v(-2124.33, -1231.14) * mm, "end": v(-1071.83, -1219.78) * mm});
            skLineSegment(sketch, "E61.39.0", {"start": v(-1010, -860) * mm, "end": v(-1010, -1157.29) * mm});
            skLineSegment(sketch, "E61.39.2", {"start": v(-1010, -1157.29) * mm, "end": v(-1010, -860) * mm});
            skLineSegment(sketch, "E61.40.0", {"start": v(-250, -797.5) * mm, "end": v(-947.5, -797.5) * mm});
            skLineSegment(sketch, "E61.40.2", {"start": v(-947.5, -797.5) * mm, "end": v(-250, -797.5) * mm});
            skLineSegment(sketch, "E61.41.0", {"start": v(-187.5, -937.5) * mm, "end": v(-187.5, -860) * mm});
            skLineSegment(sketch, "E61.41.2", {"start": v(-187.5, -860) * mm, "end": v(-187.5, -937.5) * mm});
            skLineSegment(sketch, "E61.42.0", {"start": v(-2062.5, -987.81) * mm, "end": v(-2062.5, -610) * mm});
            skLineSegment(sketch, "E61.42.2", {"start": v(-2062.5, -987.81) * mm, "end": v(-2062.5, -610) * mm});
            skSolve(sketch);
        }
        {
            var Q0;
            Q0=sQuery(id+"F6.wireOp",VERTEX,"E50.0.end");
            var Q1;
            Q1=sQuery(id+"F6.wireOp",EDGE,"E50.0");
            cPlane(context, id + "F9", {"entities" : qUnion([Q0, Q1]), "cplaneType" : CPlaneType.LINE_POINT, "offset" : 25 * mm, "width" : 150 * mm, "height" : 150 * mm});
        }
        {
            var Q0;
            Q0=qCreatedBy(id+"F9.planeOp",FACE);
            var sketch = newSketch(context, id + "F10", { "sketchPlane" : qUnion([Q0])});
            skCircle(sketch, "E62", {"center": v(-82.5, 2.5) * mm, "radius": 2.5 * mm});
            skSolve(sketch);
        }
        {
            var Q0;
            Q0=makeQuery(id+"F10.imprint","IMPRINT",FACE,{"disambiguationData":[TD([[makeQuery(id+"F10.imprint","IMPRINT",EDGE,{"derivedFrom":sQuery(id+"F10.wireOp",EDGE,"E62")}),1.0]])]});
            var Q1;
            Q1 = qConstructionFilter(qBodyType(qCreatedBy(id + "F6" ,EDGE), BodyType.WIRE), ConstructionObject.NO);
            sweep(context, id + "F11", {"profiles" : qUnion([Q0]), "path" : qUnion([Q1])});
        }
        {
            var Q0;
            Q0=qCreatedBy(makeId("Top.planeOp"),FACE);
            cPlane(context, id + "F12", {"entities" : qUnion([Q0]), "cplaneType" : CPlaneType.OFFSET, "offset" : 2500 * mm, "width" : 150 * mm, "height" : 150 * mm});
        }
        {
            var Q0;
            Q0=qCreatedBy(id+"F12.planeOp",FACE);
            var sketch = newSketch(context, id + "F13", { "sketchPlane" : qUnion([Q0])});
            skPoint(sketch, "E63", {"position": v(-156.96, -206.87) * mm});
            skPoint(sketch, "E64", {"position": v(-1260.18, -206.87) * mm});
            skPoint(sketch, "E65", {"position": v(-1765.1, -877.28) * mm});
            skPoint(sketch, "E66", {"position": v(-1260.18, -877.28) * mm});
            skPoint(sketch, "E67", {"position": v(-776.46, -643.9) * mm});
            skSolve(sketch);
        }
        {
            var Q0;
            Q0=qCreatedBy(makeId("Top.planeOp"),FACE);
            var sketch = newSketch(context, id + "F14", { "sketchPlane" : qUnion([Q0])});
            skLineSegment(sketch, "E68.0", {"start": v(-2250, -485) * mm, "end": v(-2250, -1295) * mm});
            skLineSegment(sketch, "E69.0", {"start": v(-1970, -485) * mm, "end": v(-2250, -485) * mm});
            skLineSegment(sketch, "E70.0", {"start": v(-1970, 0) * mm, "end": v(-1970, -485) * mm});
            skLineSegment(sketch, "E71.0", {"start": v(0, 0) * mm, "end": v(-1970, 0) * mm});
            skLineSegment(sketch, "E72.0", {"start": v(0, -860) * mm, "end": v(0, 0) * mm});
            skLineSegment(sketch, "E73.0", {"start": v(-860, -860) * mm, "end": v(0, -860) * mm});
            skLineSegment(sketch, "E74.0", {"start": v(-860, -1280) * mm, "end": v(-860, -860) * mm});
            skLineSegment(sketch, "E75", {"start": v(-2250, -1295) * mm, "end": v(-1510, -1287.01) * mm});
            skLineSegment(sketch, "E76", {"start": v(-860, -1280) * mm, "end": v(-910, -1280.54) * mm});
            skSolve(sketch);
        }
        {
            var Q0;
            Q0 = qSketchRegion(id + "F14", true);
            var Q1;
            Q1 = qConstructionFilter(qBodyType(qCreatedBy(id + "F14" ,EDGE), BodyType.WIRE), ConstructionObject.NO);
            var Q2;
            Q2=qCreatedBy(id+"F12.planeOp",FACE);
            extrude(context, id + "F15", {"entities" : qUnion([Q0]), "bodyType" : ExtendedToolBodyType.SURFACE, "surfaceEntities" : qUnion([Q1]), "endBound" : BoundingType.UP_TO_SURFACE, "endBoundEntityFace" : qUnion([Q2]), "depth" : 25 * mm});
        }
        {
            var Q0;
            Q0=makeQuery(id+"F15.opExtrude","SWEPT_FACE",FACE,{"disambiguationData":[OSD([sQuery(id+"F14.wireOp",EDGE,"E72.0")])]});
            var Q1;
            Q1=sQuery(id+"F13.wireOp",VERTEX,"E63");
            cPlane(context, id + "F16", {"entities" : qUnion([Q0, Q1]), "cplaneType" : CPlaneType.PLANE_POINT, "offset" : 25 * mm, "width" : 150 * mm, "height" : 150 * mm});
        }
        {
            var Q0;
            Q0=qCreatedBy(id+"F16.planeOp",FACE);
            var sketch = newSketch(context, id + "F17", { "sketchPlane" : qUnion([Q0])});
            skLineSegment(sketch, "E77", {"start": v(-206.87, 2500) * mm, "end": v(-206.87, 0) * mm, "construction": true});
            skLineSegment(sketch, "E78", {"start": v(-206.87, 2500) * mm, "end": v(233.95, 0) * mm});
            skLineSegment(sketch, "E79", {"start": v(233.95, 0) * mm, "end": v(-206.87, 0) * mm});
            skLineSegment(sketch, "E80", {"start": v(-206.87, 2500) * mm, "end": v(-647.68, 0) * mm, "construction": true});
            skLineSegment(sketch, "E81", {"start": v(-647.68, 0) * mm, "end": v(-206.87, 0) * mm, "construction": true});
            skLineSegment(sketch, "E82", {"start": v(-206.87, 0) * mm, "end": v(-206.87, 2500) * mm});
            skSolve(sketch);
        }
        {
            var Q0;
            Q0=makeQuery(id+"F17.imprint","IMPRINT",FACE,{"disambiguationData":[TD([[makeQuery(id+"F17.imprint","IMPRINT",EDGE,{"derivedFrom":sQuery(id+"F17.wireOp",EDGE,"E78")}),-1.0]])]});
            var Q1;
            Q1=sQuery(id+"F17.wireOp",EDGE,"E82");
            revolve(context, id + "F18", {"entities" : qUnion([Q0]), "axis" : qUnion([Q1]), "revolveType" : RevolveType.FULL});
        }
        {
            var Q0;
            Q0=makeQuery(id+"F1.opExtrude","CAP_FACE",FACE,{"disambiguationData":[OSD([sQuery(id+"F0.wireOp",EDGE,"E0"),sQuery(id+"F0.wireOp",EDGE,"E1"),sQuery(id+"F0.wireOp",EDGE,"E2"),sQuery(id+"F0.wireOp",EDGE,"E3"),sQuery(id+"F0.wireOp",EDGE,"E4"),sQuery(id+"F0.wireOp",EDGE,"E5"),sQuery(id+"F0.wireOp",EDGE,"E6"),sQuery(id+"F0.wireOp",EDGE,"E7")])],"isStart":true});
            var sketch = newSketch(context, id + "F19", { "sketchPlane" : qUnion([Q0])});
            skLineSegment(sketch, "E83.bottom", {"start": v(-200, -260) * mm, "end": v(-500, -260) * mm});
            skLineSegment(sketch, "E83.top", {"start": v(-200, -560) * mm, "end": v(-500, -560) * mm});
            skLineSegment(sketch, "E83.left", {"start": v(-500, -260) * mm, "end": v(-500, -560) * mm});
            skLineSegment(sketch, "E83.right", {"start": v(-200, -260) * mm, "end": v(-200, -560) * mm});
            skLineSegment(sketch, "E84", {"start": v(-350, -260) * mm, "end": v(-350, -560) * mm, "construction": true});
            skLineSegment(sketch, "E85", {"start": v(-350, -560) * mm, "end": v(-350, -410) * mm});
            skLineSegment(sketch, "E86", {"start": v(-500, -410) * mm, "end": v(-350, -410) * mm, "construction": true});
            skSolve(sketch);
        }
        {
            var Q0;
            Q0=makeQuery(id+"F19.imprint","IMPRINT",FACE,{"disambiguationData":[TD([[makeQuery(id+"F19.imprint","IMPRINT",EDGE,{"derivedFrom":sQuery(id+"F19.wireOp",EDGE,"E83.bottom")}),1.0]])]});
            extrude(context, id + "F20", {"entities" : qUnion([Q0]), "operationType" : NewBodyOperationType.ADD, "depth" : 25 * mm, "offsetDistance" : 25 * mm});
        }
        {
            var Q0;
            Q0=qCreatedBy(id+"F9.planeOp",FACE);
            var sketch = newSketch(context, id + "F21", { "sketchPlane" : qUnion([Q0])});
            skCircle(sketch, "E87", {"center": v(-62.5, 6) * mm, "radius": 6 * mm});
            skSolve(sketch);
        }
        {
            var Q0;
            Q0=makeQuery(id+"F21.imprint","IMPRINT",FACE,{"disambiguationData":[TD([[makeQuery(id+"F21.imprint","IMPRINT",EDGE,{"derivedFrom":sQuery(id+"F21.wireOp",EDGE,"E87")}),1.0]])]});
            var Q1;
            Q1=sQuery(id+"F21.wireOp",EDGE,"E87");
            var Q2;
            Q2 = qConstructionFilter(qBodyType(qCreatedBy(id + "F6" ,EDGE), BodyType.WIRE), ConstructionObject.NO);
            sweep(context, id + "F22", {"profiles" : qUnion([Q0]), "surfaceProfiles" : qUnion([Q1]), "path" : qUnion([Q2])});
        }
    });
